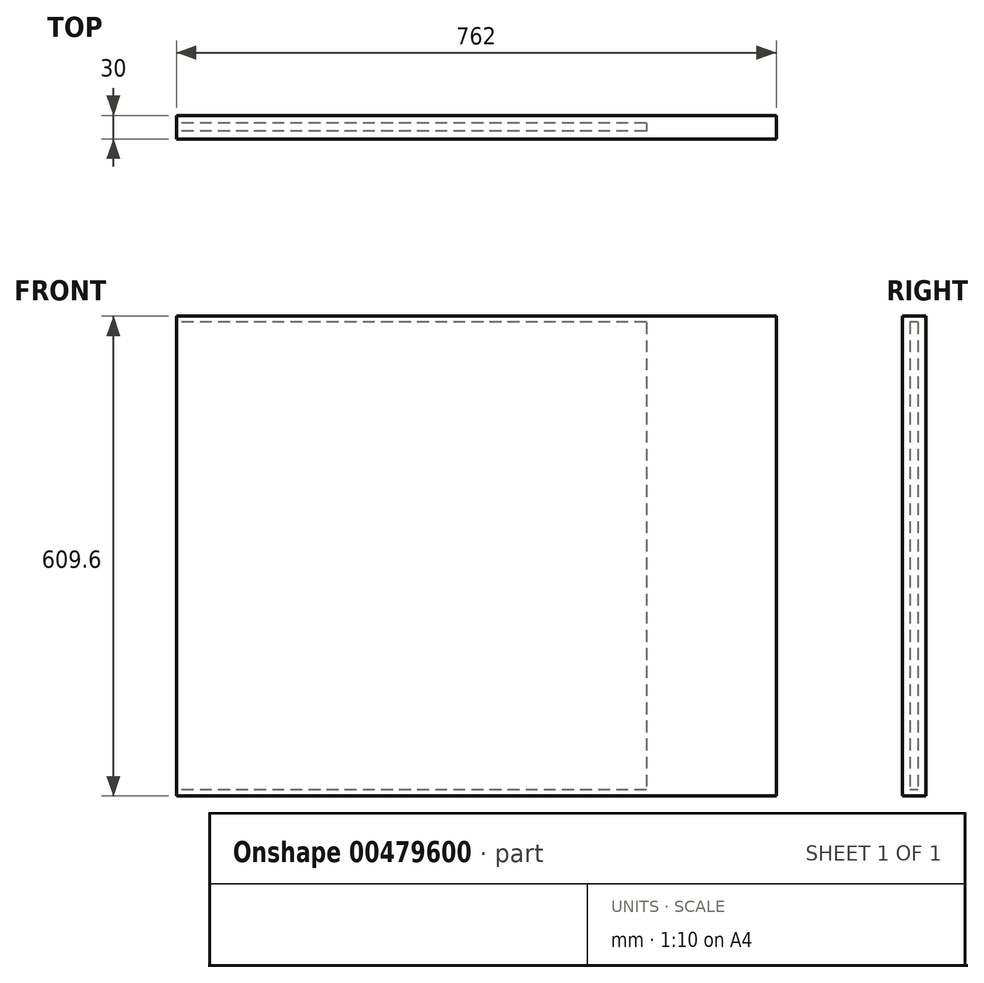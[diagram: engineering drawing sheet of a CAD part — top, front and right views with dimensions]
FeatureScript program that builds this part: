
annotation { "Feature Type Name" : "Feature", "Feature Type Description" : "" }
export const myFeature = defineFeature(function(context is Context, id is Id, definition is map)
    precondition{}
    {
        {
            var Q0;
            Q0=qCreatedBy(makeId("Front.planeOp"),FACE);
            var sketch = newSketch(context, id + "F0", { "sketchPlane" : qUnion([Q0])});
            skLineSegment(sketch, "E0.bottom", {"start": v(381, -304.8) * mm, "end": v(-381, -304.8) * mm});
            skLineSegment(sketch, "E0.top", {"start": v(381, 304.8) * mm, "end": v(-381, 304.8) * mm});
            skLineSegment(sketch, "E0.left", {"start": v(381, -304.8) * mm, "end": v(381, 304.8) * mm});
            skLineSegment(sketch, "E0.right", {"start": v(-381, -304.8) * mm, "end": v(-381, 304.8) * mm});
            skPoint(sketch, "E0.middle", {"position": v(0, 0) * mm});
            skSolve(sketch);
        }
        {
            var Q0;
            Q0=makeQuery(id+"F0.imprint","IMPRINT",FACE,{"disambiguationData":[TD([[makeQuery(id+"F0.imprint","IMPRINT",EDGE,{"derivedFrom":sQuery(id+"F0.wireOp",EDGE,"E0.bottom")}),-1.0]])]});
            extrude(context, id + "F1", {"entities" : qUnion([Q0]), "depth" : 30 * mm});
        }
        {
            var Q0;
            Q0=makeQuery(id+"F1.opExtrude","SWEPT_FACE",FACE,{"disambiguationData":[OSD([sQuery(id+"F0.wireOp",EDGE,"E0.right")])]});
            var sketch = newSketch(context, id + "F2", { "sketchPlane" : qUnion([Q0])});
            skLineSegment(sketch, "E1.bottom", {"start": v(10, 297.18) * mm, "end": v(20, 297.18) * mm});
            skLineSegment(sketch, "E1.top", {"start": v(10, -297.18) * mm, "end": v(20, -297.18) * mm});
            skLineSegment(sketch, "E1.left", {"start": v(10, 297.18) * mm, "end": v(10, -297.18) * mm});
            skLineSegment(sketch, "E1.right", {"start": v(20, 297.18) * mm, "end": v(20, -297.18) * mm});
            skSolve(sketch);
        }
        {
            var Q0;
            Q0=makeQuery(id+"F2.imprint","IMPRINT",FACE,{"disambiguationData":[TD([[makeQuery(id+"F2.imprint","IMPRINT",EDGE,{"derivedFrom":sQuery(id+"F2.wireOp",EDGE,"E1.bottom")}),-1.0]])]});
            extrude(context, id + "F3", {"entities" : qUnion([Q0]), "operationType" : NewBodyOperationType.REMOVE, "oppositeDirection" : true, "depth" : 596.9 * mm});
        }
    });
